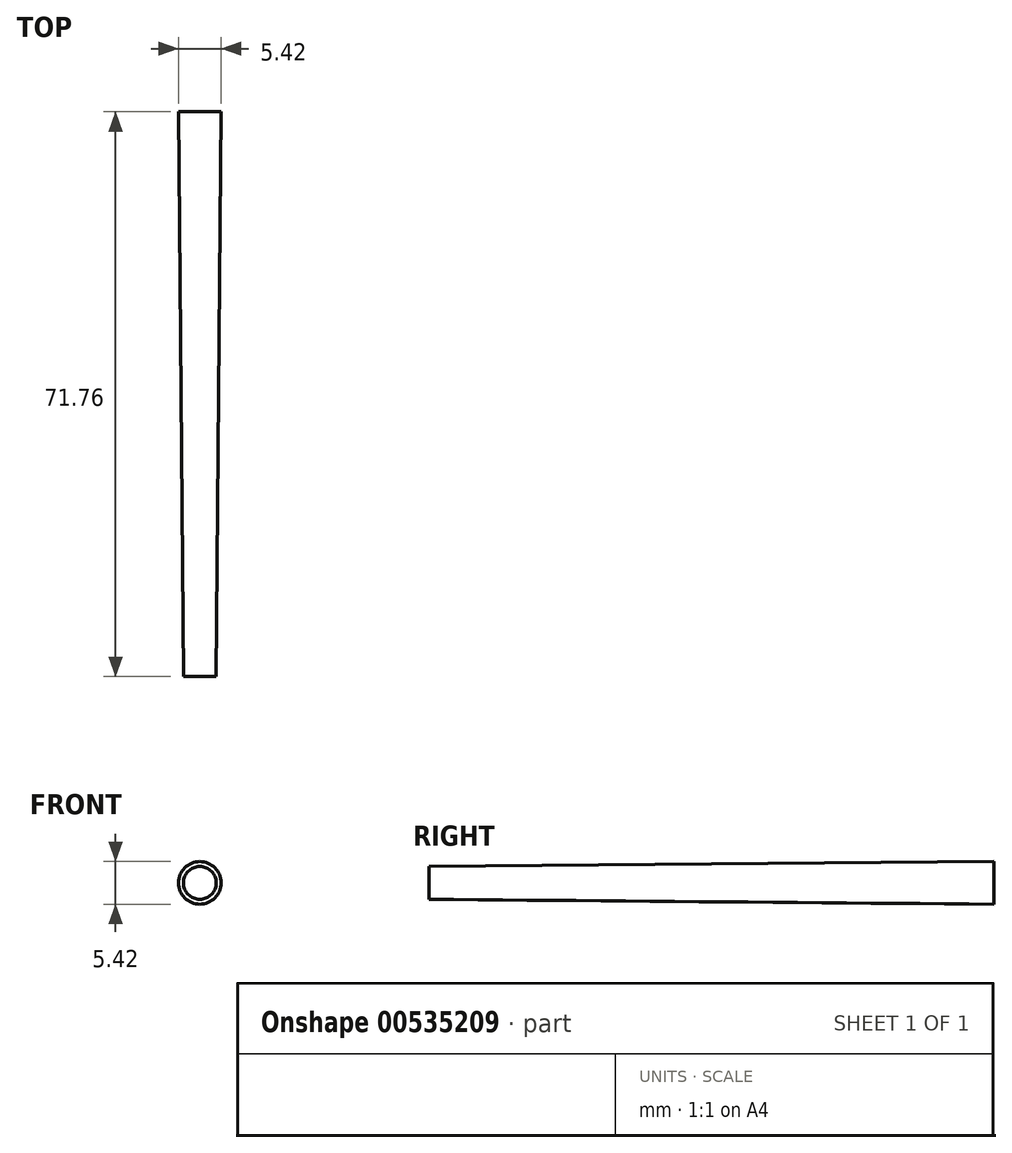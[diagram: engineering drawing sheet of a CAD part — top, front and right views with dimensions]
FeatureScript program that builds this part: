
annotation { "Feature Type Name" : "Feature", "Feature Type Description" : "" }
export const myFeature = defineFeature(function(context is Context, id is Id, definition is map)
    precondition{}
    {
        {
            var Q0;
            Q0=qCreatedBy(makeId("Front.planeOp"),FACE);
            var sketch = newSketch(context, id + "F0", { "sketchPlane" : qUnion([Q0])});
            skCircle(sketch, "E0", {"center": v(0, 0) * mm, "radius": 2.7 * mm});
            skSolve(sketch);
        }
        {
            var Q0;
            Q0=makeQuery(id+"F0.imprint","IMPRINT",FACE,{"disambiguationData":[TD([[makeQuery(id+"F0.imprint","IMPRINT",EDGE,{"derivedFrom":sQuery(id+"F0.wireOp",EDGE,"E0")}),1.0]])]});
            extrude(context, id + "F1", {"entities" : qUnion([Q0]), "depth" : 71.75 * mm, "offsetDistance" : 25.4 * mm, "hasDraft" : true, "draftAngle" : .5 * degree, "draftPullDirection" : true});
        }
    });
